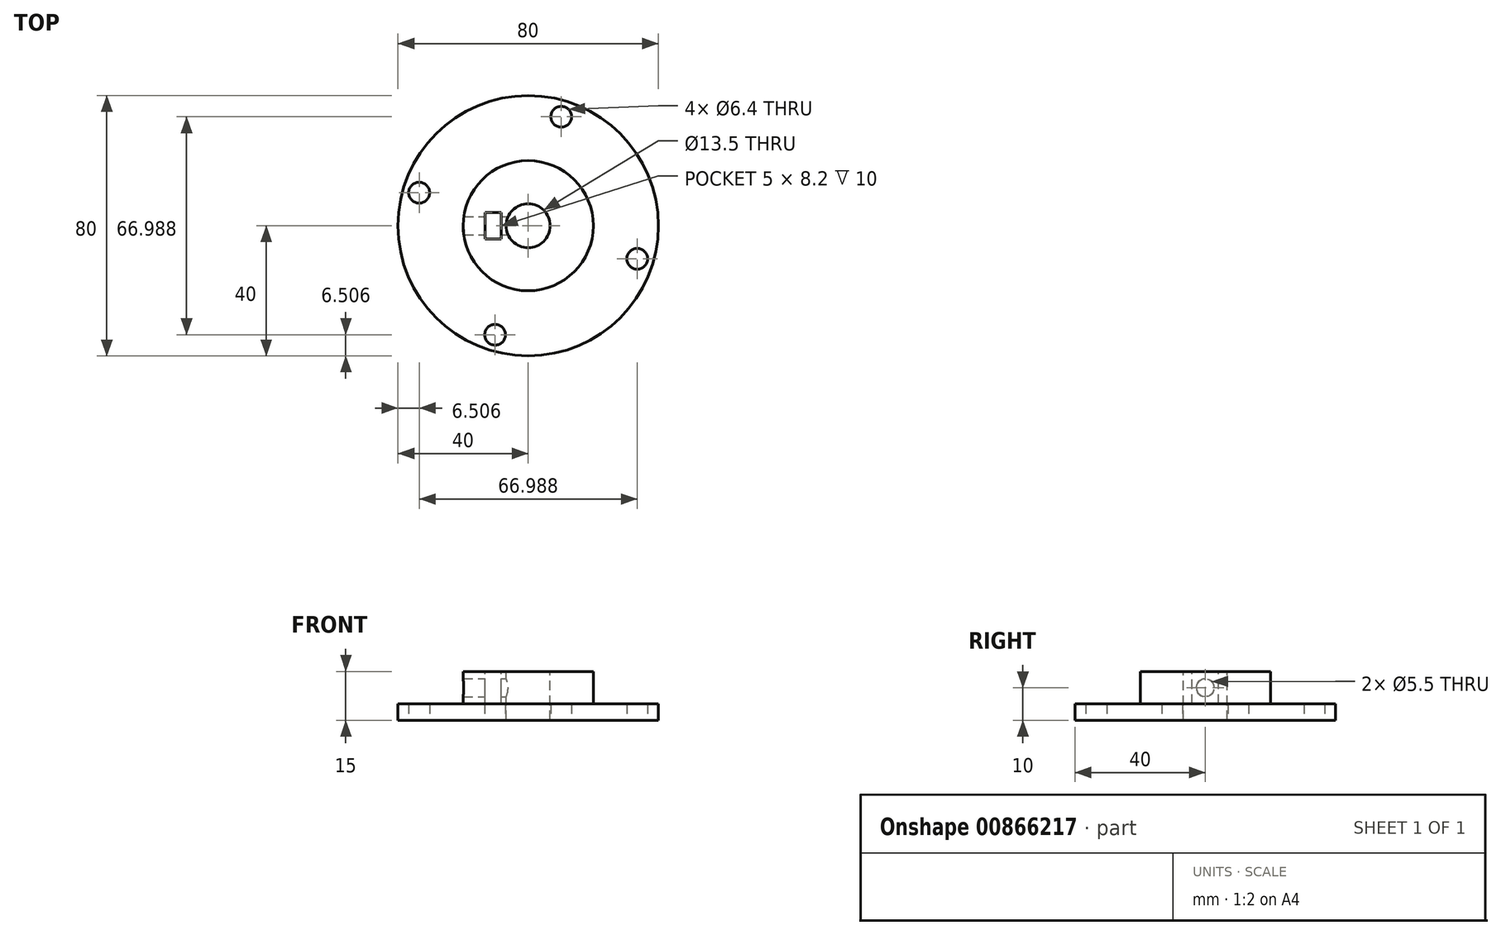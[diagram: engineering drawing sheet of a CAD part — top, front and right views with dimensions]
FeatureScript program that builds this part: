
annotation { "Feature Type Name" : "Feature", "Feature Type Description" : "" }
export const myFeature = defineFeature(function(context is Context, id is Id, definition is map)
    precondition{}
    {
        {
            var Q0;
            Q0=qCreatedBy(makeId("Top.planeOp"),FACE);
            var sketch = newSketch(context, id + "F0", { "sketchPlane" : qUnion([Q0])});
            skCircle(sketch, "E0", {"center": v(0, 0) * mm, "radius": 40 * mm});
            skCircle(sketch, "E1", {"center": v(10.16, 33.5) * mm, "radius": 3.2 * mm});
            skCircle(sketch, "E2.1.0", {"center": v(-33.5, 10.16) * mm, "radius": 3.2 * mm});
            skCircle(sketch, "E2.2.0", {"center": v(-10.16, -33.5) * mm, "radius": 3.2 * mm});
            skCircle(sketch, "E2.3.0", {"center": v(33.5, -10.16) * mm, "radius": 3.2 * mm});
            skSolve(sketch);
        }
        {
            var Q0;
            Q0=makeQuery(id+"F0.imprint","IMPRINT",FACE,{"disambiguationData":[TD([[makeQuery(id+"F0.imprint","IMPRINT",EDGE,{"derivedFrom":sQuery(id+"F0.wireOp",EDGE,"E0")}),1.0]])]});
            extrude(context, id + "F1", {"entities" : qUnion([Q0]), "depth" : 5 * mm, "offsetDistance" : 25 * mm});
        }
        {
            var Q0;
            Q0=makeQuery(id+"F1.opExtrude","CAP_FACE",FACE,{"disambiguationData":[OSD([sQuery(id+"F0.wireOp",EDGE,"E0"),sQuery(id+"F0.wireOp",EDGE,"E1"),sQuery(id+"F0.wireOp",EDGE,"E2.1.0"),sQuery(id+"F0.wireOp",EDGE,"E2.2.0"),sQuery(id+"F0.wireOp",EDGE,"E2.3.0")])],"isStart":false});
            var sketch = newSketch(context, id + "F2", { "sketchPlane" : qUnion([Q0])});
            skCircle(sketch, "E3", {"center": v(0, 0) * mm, "radius": 20 * mm});
            skSolve(sketch);
        }
        {
            var Q0;
            Q0=makeQuery(id+"F2.imprint","IMPRINT",FACE,{"disambiguationData":[TD([[makeQuery(id+"F2.imprint","IMPRINT",EDGE,{"derivedFrom":sQuery(id+"F2.wireOp",EDGE,"E3")}),1.0]])]});
            extrude(context, id + "F3", {"entities" : qUnion([Q0]), "operationType" : NewBodyOperationType.ADD, "depth" : 10 * mm, "offsetDistance" : 25 * mm});
        }
        {
            var Q0;
            Q0=makeQuery(id+"F3.opExtrude","CAP_FACE",FACE,{"disambiguationData":[OSD([sQuery(id+"F2.wireOp",EDGE,"E3")])],"isStart":false});
            var sketch = newSketch(context, id + "F4", { "sketchPlane" : qUnion([Q0])});
            skCircle(sketch, "E4", {"center": v(0, 0) * mm, "radius": 6.75 * mm});
            skSolve(sketch);
        }
        {
            var Q0;
            Q0=makeQuery(id+"F4.imprint","IMPRINT",FACE,{"disambiguationData":[TD([[makeQuery(id+"F4.imprint","IMPRINT",EDGE,{"derivedFrom":sQuery(id+"F4.wireOp",EDGE,"E4")}),1.0]])]});
            extrude(context, id + "F5", {"entities" : qUnion([Q0]), "operationType" : NewBodyOperationType.REMOVE, "endBound" : BoundingType.THROUGH_ALL, "oppositeDirection" : true, "depth" : 25 * mm, "offsetDistance" : 25 * mm});
        }
        {
            var Q0;
            Q0=qCreatedBy(makeId("Right.planeOp"),FACE);
            var sketch = newSketch(context, id + "F6", { "sketchPlane" : qUnion([Q0])});
            skCircle(sketch, "E5", {"center": v(0, 10) * mm, "radius": 2.75 * mm});
            skSolve(sketch);
        }
        {
            var Q0;
            Q0=makeQuery(id+"F6.imprint","IMPRINT",FACE,{"disambiguationData":[TD([[makeQuery(id+"F6.imprint","IMPRINT",EDGE,{"derivedFrom":sQuery(id+"F6.wireOp",EDGE,"E5")}),1.0]])]});
            extrude(context, id + "F7", {"entities" : qUnion([Q0]), "operationType" : NewBodyOperationType.REMOVE, "oppositeDirection" : true, "depth" : 25 * mm, "offsetDistance" : 25 * mm});
        }
        {
            var Q0;
            Q0=makeQuery(id+"F3.opExtrude","CAP_FACE",FACE,{"disambiguationData":[OSD([sQuery(id+"F2.wireOp",EDGE,"E3")])],"isStart":false});
            var sketch = newSketch(context, id + "F8", { "sketchPlane" : qUnion([Q0])});
            skLineSegment(sketch, "E6.bottom", {"start": v(-13.25, -4.1) * mm, "end": v(-8.25, -4.1) * mm});
            skLineSegment(sketch, "E6.top", {"start": v(-13.25, 4.1) * mm, "end": v(-8.25, 4.1) * mm});
            skLineSegment(sketch, "E6.left", {"start": v(-13.25, -4.1) * mm, "end": v(-13.25, 4.1) * mm});
            skLineSegment(sketch, "E6.right", {"start": v(-8.25, -4.1) * mm, "end": v(-8.25, 4.1) * mm});
            skPoint(sketch, "E6.middle", {"position": v(-10.75, 0) * mm});
            skSolve(sketch);
        }
        {
            var Q0;
            Q0=makeQuery(id+"F8.imprint","IMPRINT",FACE,{"disambiguationData":[TD([[makeQuery(id+"F8.imprint","IMPRINT",EDGE,{"derivedFrom":sQuery(id+"F8.wireOp",EDGE,"E6.bottom")}),1.0]])]});
            extrude(context, id + "F9", {"entities" : qUnion([Q0]), "operationType" : NewBodyOperationType.REMOVE, "oppositeDirection" : true, "depth" : 10 * mm, "offsetDistance" : 25 * mm});
        }
    });
